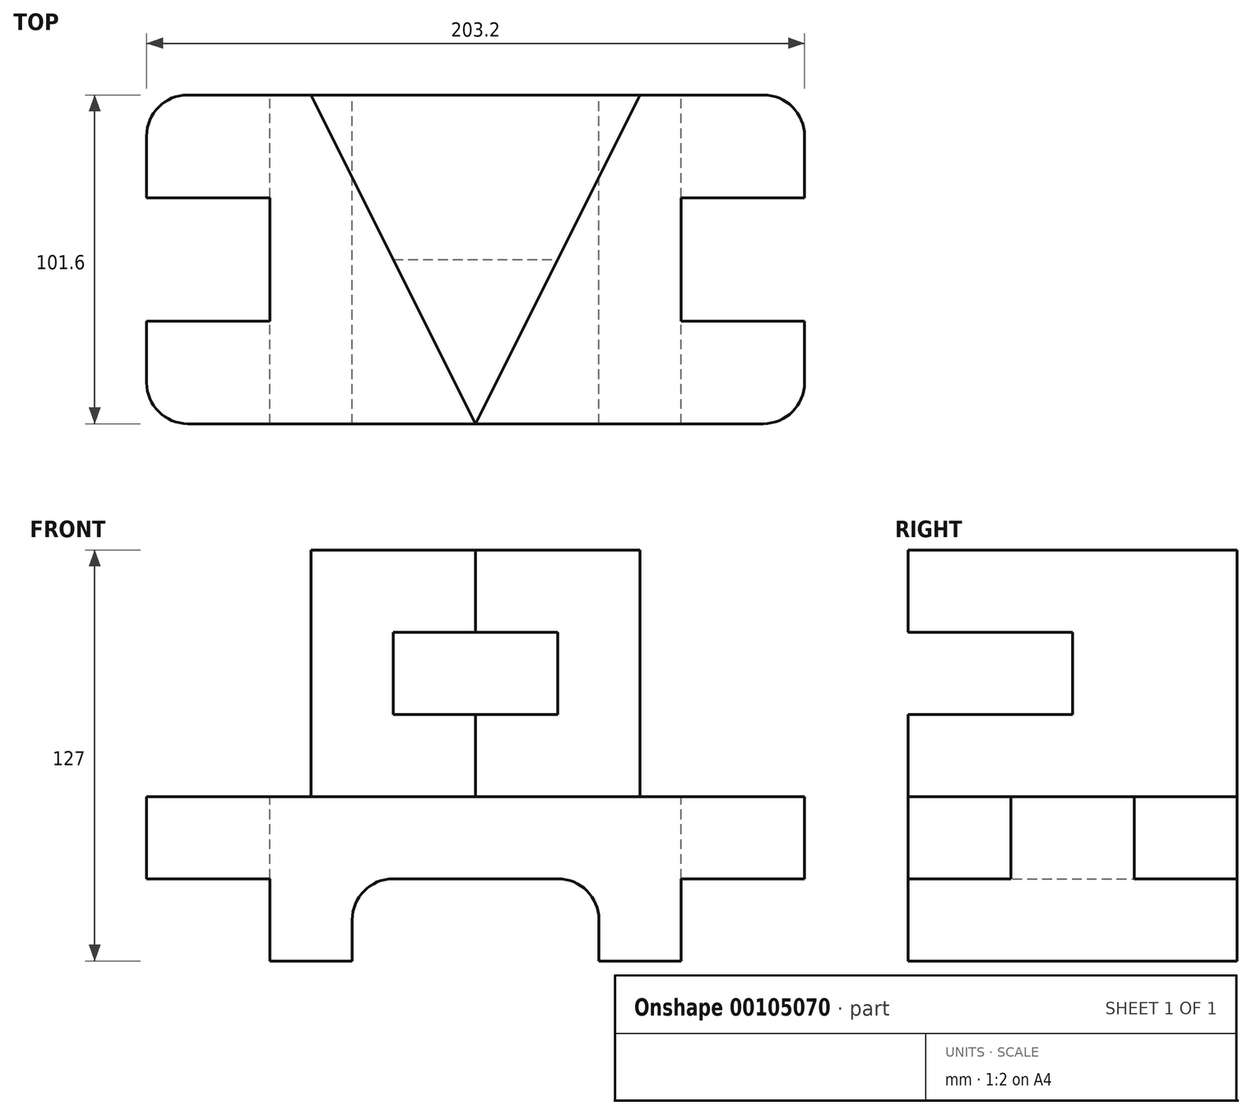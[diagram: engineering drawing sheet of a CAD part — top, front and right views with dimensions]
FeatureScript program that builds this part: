
annotation { "Feature Type Name" : "Feature", "Feature Type Description" : "" }
export const myFeature = defineFeature(function(context is Context, id is Id, definition is map)
    precondition{}
    {
        {
            var Q0;
            Q0=qCreatedBy(makeId("Front.planeOp"),FACE);
            var sketch = newSketch(context, id + "F0", { "sketchPlane" : qUnion([Q0])});
            skLineSegment(sketch, "E0", {"start": v(0, 0) * mm, "end": v(-101.6, 0) * mm});
            skLineSegment(sketch, "E1", {"start": v(-101.6, 0) * mm, "end": v(-101.6, -25.4) * mm});
            skLineSegment(sketch, "E2", {"start": v(-101.6, -25.4) * mm, "end": v(-63.5, -25.4) * mm});
            skLineSegment(sketch, "E3", {"start": v(-63.5, -25.4) * mm, "end": v(-63.5, -50.8) * mm});
            skLineSegment(sketch, "E4", {"start": v(-63.5, -50.8) * mm, "end": v(-38.1, -50.8) * mm});
            skLineSegment(sketch, "E5", {"start": v(-38.1, -50.8) * mm, "end": v(-38.1, -38.1) * mm});
            skLineSegment(sketch, "E6", {"start": v(-25.4, -25.4) * mm, "end": v(0, -25.4) * mm});
            skLineSegment(sketch, "E7", {"start": v(0, -25.4) * mm, "end": v(0, 0) * mm});
            skLineSegment(sketch, "E8.MirrorCS", {"start": v(25.4, -25.4) * mm, "end": v(0, -25.4) * mm});
            skLineSegment(sketch, "E9.MirrorCS", {"start": v(38.1, -50.8) * mm, "end": v(38.1, -38.1) * mm});
            skLineSegment(sketch, "E10.MirrorCS", {"start": v(63.5, -50.8) * mm, "end": v(38.1, -50.8) * mm});
            skLineSegment(sketch, "E11.MirrorCS", {"start": v(63.5, -25.4) * mm, "end": v(63.5, -50.8) * mm});
            skLineSegment(sketch, "E12.MirrorCS", {"start": v(101.6, -25.4) * mm, "end": v(63.5, -25.4) * mm});
            skLineSegment(sketch, "E13.MirrorCS", {"start": v(101.6, 0) * mm, "end": v(101.6, -25.4) * mm});
            skLineSegment(sketch, "E14.MirrorCS", {"start": v(0, 0) * mm, "end": v(101.6, 0) * mm});
            skPoint(sketch, "E15.visualSharp", {"position": v(-38.1, -25.4) * mm});
            skArc(sketch, "E15.filletArc", {"start": v(-25.4, -25.4) * mm, "mid": v(-34.38, -29.12) * mm, "end": v(-38.1, -38.1) * mm});
            skPoint(sketch, "E16.visualSharp", {"position": v(38.1, -25.4) * mm});
            skArc(sketch, "E16.filletArc", {"start": v(38.1, -38.1) * mm, "mid": v(34.38, -29.12) * mm, "end": v(25.4, -25.4) * mm});
            skSolve(sketch);
        }
        {
            var Q0;
            Q0=makeQuery(id+"F0.imprint","IMPRINT",FACE,{"disambiguationData":[TD([[makeQuery(id+"F0.imprint","IMPRINT",EDGE,{"derivedFrom":sQuery(id+"F0.wireOp",EDGE,"E0")}),1.0]])]});
            var Q1;
            Q1=makeQuery(id+"F0.imprint","IMPRINT",FACE,{"disambiguationData":[TD([[makeQuery(id+"F0.imprint","IMPRINT",EDGE,{"derivedFrom":sQuery(id+"F0.wireOp",EDGE,"E7")}),-1.0]])]});
            extrude(context, id + "F1", {"entities" : qUnion([Q0, Q1]), "endBound" : BoundingType.SYMMETRIC, "depth" : 101.6 * mm});
        }
        {
            var Q0;
            Q0=qCreatedBy(makeId("Top.planeOp"),FACE);
            var sketch = newSketch(context, id + "F2", { "sketchPlane" : qUnion([Q0])});
            skLineSegment(sketch, "E17.bottom", {"start": v(-101.6, -19.05) * mm, "end": v(-63.5, -19.05) * mm});
            skLineSegment(sketch, "E17.top", {"start": v(-101.6, 19.05) * mm, "end": v(-63.5, 19.05) * mm});
            skLineSegment(sketch, "E17.left", {"start": v(-101.6, -19.05) * mm, "end": v(-101.6, 19.05) * mm});
            skLineSegment(sketch, "E17.right", {"start": v(-63.5, -19.05) * mm, "end": v(-63.5, 19.05) * mm});
            skLineSegment(sketch, "E18.bottom", {"start": v(101.6, -19.05) * mm, "end": v(63.5, -19.05) * mm});
            skLineSegment(sketch, "E18.top", {"start": v(101.6, 19.05) * mm, "end": v(63.5, 19.05) * mm});
            skLineSegment(sketch, "E18.left", {"start": v(101.6, -19.05) * mm, "end": v(101.6, 19.05) * mm});
            skLineSegment(sketch, "E18.right", {"start": v(63.5, -19.05) * mm, "end": v(63.5, 19.05) * mm});
            skSolve(sketch);
        }
        {
            var Q0;
            Q0=makeQuery(id+"F2.imprint","IMPRINT",FACE,{"disambiguationData":[TD([[makeQuery(id+"F2.imprint","IMPRINT",EDGE,{"derivedFrom":sQuery(id+"F2.wireOp",EDGE,"E17.bottom")}),1.0]])]});
            var Q1;
            Q1=makeQuery(id+"F2.imprint","IMPRINT",FACE,{"disambiguationData":[TD([[makeQuery(id+"F2.imprint","IMPRINT",EDGE,{"derivedFrom":sQuery(id+"F2.wireOp",EDGE,"E18.bottom")}),-1.0]])]});
            extrude(context, id + "F3", {"entities" : qUnion([Q0, Q1]), "operationType" : NewBodyOperationType.REMOVE, "endBound" : BoundingType.THROUGH_ALL, "oppositeDirection" : true, "depth" : 25.4 * mm});
        }
        {
            var Q0;
            Q0=makeQuery(id+"F1.opExtrude","CAP_EDGE",EDGE,{"disambiguationData":[OSD([sQuery(id+"F0.wireOp",EDGE,"E13.MirrorCS")])],"isStart":false});
            var Q1;
            Q1=makeQuery(id+"F1.opExtrude","CAP_EDGE",EDGE,{"disambiguationData":[OSD([sQuery(id+"F0.wireOp",EDGE,"E13.MirrorCS")])],"isStart":true});
            var Q2;
            Q2=makeQuery(id+"F1.opExtrude","CAP_EDGE",EDGE,{"disambiguationData":[OSD([sQuery(id+"F0.wireOp",EDGE,"E1")])],"isStart":false});
            var Q3;
            Q3=makeQuery(id+"F1.opExtrude","CAP_EDGE",EDGE,{"disambiguationData":[OSD([sQuery(id+"F0.wireOp",EDGE,"E1")])],"isStart":true});
            fillet(context, id + "F4", {"entities" : qUnion([Q0, Q1, Q2, Q3]), "radius" : 12.7 * mm, "tangentPropagation" : true, "allowEdgeOverflow" : false});
        }
        {
            var Q0;
            Q0=qCreatedBy(makeId("Top.planeOp"),FACE);
            var sketch = newSketch(context, id + "F5", { "sketchPlane" : qUnion([Q0])});
            skLineSegment(sketch, "E19", {"start": v(0, -50.8) * mm, "end": v(0, 50.8) * mm});
            skLineSegment(sketch, "E20", {"start": v(0, 50.8) * mm, "end": v(50.8, 50.8) * mm});
            skLineSegment(sketch, "E21", {"start": v(50.8, 50.8) * mm, "end": v(0, -50.8) * mm});
            skPoint(sketch, "E22.MirrorCS.end.orphan", {"position": v(0, -50.8) * mm});
            skPoint(sketch, "E23.MirrorCS.start.orphan", {"position": v(0, 50.8) * mm});
            skLineSegment(sketch, "E24.MirrorCS", {"start": v(0, 50.8) * mm, "end": v(-50.8, 50.8) * mm});
            skLineSegment(sketch, "E25.MirrorCS", {"start": v(-50.8, 50.8) * mm, "end": v(0, -50.8) * mm});
            skSolve(sketch);
        }
        {
            var Q0;
            Q0=qCreatedBy(makeId("Right.planeOp"),FACE);
            var sketch = newSketch(context, id + "F6", { "sketchPlane" : qUnion([Q0])});
            skLineSegment(sketch, "E26.bottom", {"start": v(0, 25.4) * mm, "end": v(-50.8, 25.4) * mm});
            skLineSegment(sketch, "E26.top", {"start": v(0, 50.8) * mm, "end": v(-50.8, 50.8) * mm});
            skLineSegment(sketch, "E26.left", {"start": v(0, 25.4) * mm, "end": v(0, 50.8) * mm});
            skLineSegment(sketch, "E26.right", {"start": v(-50.8, 25.4) * mm, "end": v(-50.8, 50.8) * mm});
            skSolve(sketch);
        }
        {
            var Q0;
            Q0=makeQuery(id+"F5.imprint","IMPRINT",FACE,{"disambiguationData":[TD([[makeQuery(id+"F5.imprint","IMPRINT",EDGE,{"derivedFrom":sQuery(id+"F5.wireOp",EDGE,"E19")}),-1.0]])]});
            extrude(context, id + "F7", {"entities" : qUnion([Q0]), "operationType" : NewBodyOperationType.ADD, "depth" : 76.2 * mm});
        }
        {
            var Q0;
            Q0=makeQuery(id+"F5.imprint","IMPRINT",FACE,{"disambiguationData":[TD([[makeQuery(id+"F5.imprint","IMPRINT",EDGE,{"derivedFrom":sQuery(id+"F5.wireOp",EDGE,"E19")}),1.0]])]});
            extrude(context, id + "F8", {"entities" : qUnion([Q0]), "operationType" : NewBodyOperationType.ADD, "depth" : 76.2 * mm});
        }
        {
            var Q0;
            Q0=makeQuery(id+"F6.imprint","IMPRINT",FACE,{"disambiguationData":[TD([[makeQuery(id+"F6.imprint","IMPRINT",EDGE,{"derivedFrom":sQuery(id+"F6.wireOp",EDGE,"E26.bottom")}),-1.0]])]});
            extrude(context, id + "F9", {"entities" : qUnion([Q0]), "operationType" : NewBodyOperationType.REMOVE, "endBound" : BoundingType.SYMMETRIC, "oppositeDirection" : true, "depth" : 101.6 * mm});
        }
    });
